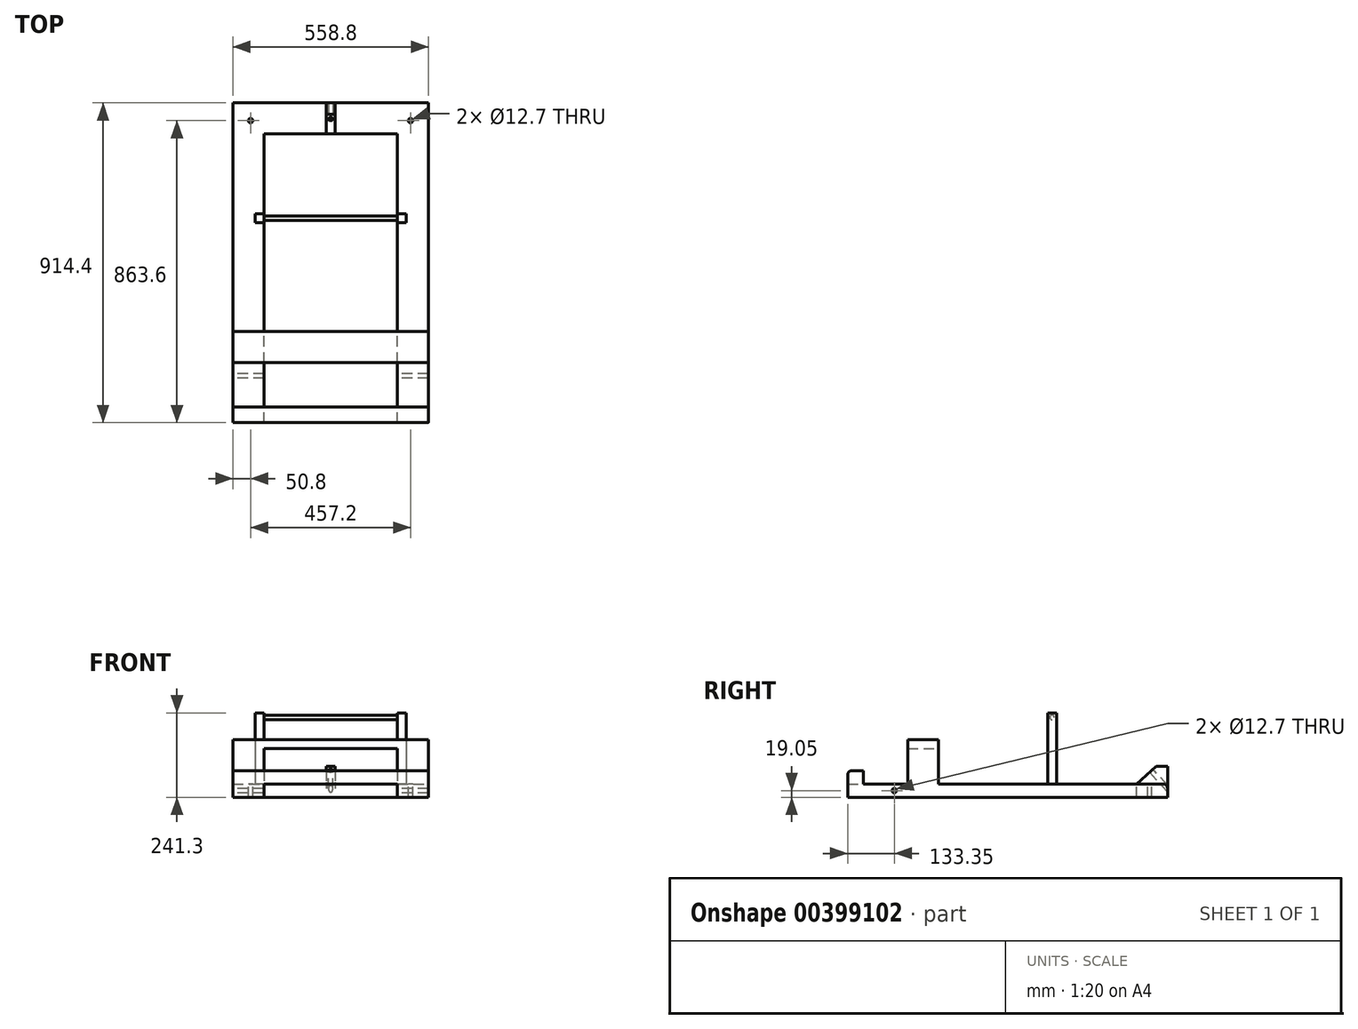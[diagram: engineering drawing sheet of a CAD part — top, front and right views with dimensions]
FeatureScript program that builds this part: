
annotation { "Feature Type Name" : "Feature", "Feature Type Description" : "" }
export const myFeature = defineFeature(function(context is Context, id is Id, definition is map)
    precondition{}
    {
        {
            var Q0;
            Q0=qCreatedBy(makeId("Right.planeOp"),FACE);
            var sketch = newSketch(context, id + "F0", { "sketchPlane" : qUnion([Q0])});
            skLineSegment(sketch, "E0.bottom", {"start": v(0, 0) * mm, "end": v(914.4, 0) * mm});
            skLineSegment(sketch, "E0.top", {"start": v(0, 38.1) * mm, "end": v(914.4, 38.1) * mm});
            skLineSegment(sketch, "E0.left", {"start": v(0, 0) * mm, "end": v(0, 38.1) * mm});
            skLineSegment(sketch, "E0.right", {"start": v(914.4, 0) * mm, "end": v(914.4, 38.1) * mm});
            skSolve(sketch);
        }
        {
            var Q0;
            Q0=makeQuery(id+"F0.imprint","IMPRINT",FACE,{"disambiguationData":[TD([[makeQuery(id+"F0.imprint","IMPRINT",EDGE,{"derivedFrom":sQuery(id+"F0.wireOp",EDGE,"E0.bottom")}),1.0]])]});
            extrude(context, id + "F1", {"entities" : qUnion([Q0]), "depth" : 88.9 * mm});
        }
        {
            var Q0;
            Q0=makeQuery(id+"F1.opExtrude","SWEPT_FACE",FACE,{"disambiguationData":[OSD([sQuery(id+"F0.wireOp",EDGE,"E0.top")])]});
            var sketch = newSketch(context, id + "F2", { "sketchPlane" : qUnion([Q0])});
            skLineSegment(sketch, "E1.bottom", {"start": v(88.9, 0) * mm, "end": v(-469.9, 0) * mm});
            skLineSegment(sketch, "E1.top", {"start": v(88.9, 44.45) * mm, "end": v(-469.9, 44.45) * mm});
            skLineSegment(sketch, "E1.left", {"start": v(88.9, 0) * mm, "end": v(88.9, 44.45) * mm});
            skLineSegment(sketch, "E1.right", {"start": v(-469.9, 0) * mm, "end": v(-469.9, 44.45) * mm});
            skSolve(sketch);
        }
        {
            var Q0;
            {var subQ4=sQuery(id+"F2.wireOp",EDGE,"E1.left");Q0=makeQuery(id+"F2.imprint","IMPRINT",FACE,{"disambiguationData":[TD([[makeQuery(id+"F2.imprint","IMPRINT",EDGE,{"derivedFrom":subQ4}),1.0]])]});}
            var Q1;
            {var subQ3=sQuery(id+"F2.wireOp",EDGE,"E1.right");Q1=makeQuery(id+"F2.imprint","IMPRINT",FACE,{"disambiguationData":[TD([[makeQuery(id+"F2.imprint","IMPRINT",EDGE,{"derivedFrom":subQ3}),-1.0]])]});}
            extrude(context, id + "F3", {"entities" : qUnion([Q0, Q1]), "operationType" : NewBodyOperationType.ADD, "depth" : 38.1 * mm});
        }
        {
            var Q0;
            Q0=makeQuery(id+"F3.opExtrude","CAP_FACE",FACE,{"disambiguationData":[OSD([sQuery(id+"F2.wireOp",EDGE,"E1.bottom"),sQuery(id+"F2.wireOp",EDGE,"E1.top"),sQuery(id+"F2.wireOp",EDGE,"E1.left"),sQuery(id+"F2.wireOp",EDGE,"E1.right")])],"isStart":true});
            var sketch = newSketch(context, id + "F4", { "sketchPlane" : qUnion([Q0])});
            skLineSegment(sketch, "E2.bottom", {"start": v(-469.9, 0) * mm, "end": v(-381, 0) * mm});
            skLineSegment(sketch, "E2.top", {"start": v(-469.9, -914.4) * mm, "end": v(-381, -914.4) * mm});
            skLineSegment(sketch, "E2.left", {"start": v(-469.9, 0) * mm, "end": v(-469.9, -914.4) * mm});
            skLineSegment(sketch, "E2.right", {"start": v(-381, 0) * mm, "end": v(-381, -914.4) * mm});
            skSolve(sketch);
        }
        {
            var Q0;
            {var subQ0=sQuery(id+"F4.wireOp",EDGE,"E2.bottom");Q0=makeQuery(id+"F4.imprint","IMPRINT",FACE,{"disambiguationData":[TD([[makeQuery(id+"F4.imprint","IMPRINT",EDGE,{"derivedFrom":subQ0}),1.0]])]});}
            var Q1;
            {var subQ0=sQuery(id+"F4.wireOp",EDGE,"E2.top");Q1=makeQuery(id+"F4.imprint","IMPRINT",FACE,{"disambiguationData":[TD([[makeQuery(id+"F4.imprint","IMPRINT",EDGE,{"derivedFrom":subQ0}),1.0]])]});}
            extrude(context, id + "F5", {"entities" : qUnion([Q0, Q1]), "operationType" : NewBodyOperationType.ADD, "depth" : 38.1 * mm});
        }
        {
            var Q0;
            Q0=makeQuery(id+"F5.boolean.opBoolean","MERGE",FACE,{"derivedFrom":[makeQuery(id+"F3.opExtrude","SWEPT_FACE",FACE,{"disambiguationData":[OSD([sQuery(id+"F2.wireOp",EDGE,"E1.right")])]}),makeQuery(id+"F5.opExtrude","SWEPT_FACE",FACE,{"disambiguationData":[OSD([sQuery(id+"F4.wireOp",EDGE,"E2.left")])]})]});
            var sketch = newSketch(context, id + "F6", { "sketchPlane" : qUnion([Q0])});
            skCircle(sketch, "E3", {"center": v(-133.35, 19.05) * mm, "radius": 6.35 * mm});
            skSolve(sketch);
        }
        {
            var Q0;
            Q0=makeQuery(id+"F6.imprint","IMPRINT",FACE,{"disambiguationData":[TD([[makeQuery(id+"F6.imprint","IMPRINT",EDGE,{"derivedFrom":sQuery(id+"F6.wireOp",EDGE,"E3")}),1.0]])]});
            var Q1;
            Q1=sQuery(id+"F6.wireOp",EDGE,"E3");
            extrude(context, id + "F7", {"entities" : qUnion([Q0]), "operationType" : NewBodyOperationType.REMOVE, "surfaceEntities" : qUnion([Q1]), "endBound" : BoundingType.THROUGH_ALL, "oppositeDirection" : true, "depth" : 25.4 * mm});
        }
        {
            var Q0;
            Q0=makeQuery(id+"F1.opExtrude","SWEPT_FACE",FACE,{"disambiguationData":[OSD([sQuery(id+"F0.wireOp",EDGE,"E0.top")])]});
            var sketch = newSketch(context, id + "F8", { "sketchPlane" : qUnion([Q0])});
            skSolve(sketch);
        }
        {
            var Q0;
            {var subQ0=sQuery(id+"F0.wireOp",EDGE,"E0.top");Q0=makeQuery(id+"F8.imprint","IMPRINT",FACE,{"disambiguationData":[TD([[makeQuery(id+"F8.imprint","IMPRINT",EDGE,{"derivedFrom":makeQuery(id+"F1.opExtrude","CAP_EDGE",EDGE,{"disambiguationData":[OSD([subQ0])],"isStart":false})}),1.0]])]});}
            var sketch = newSketch(context, id + "F9", { "sketchPlane" : qUnion([Q0])});
            skLineSegment(sketch, "E4.bottom", {"start": v(25.4, 571.5) * mm, "end": v(0, 571.5) * mm});
            skLineSegment(sketch, "E4.top", {"start": v(25.4, 596.9) * mm, "end": v(0, 596.9) * mm});
            skLineSegment(sketch, "E4.left", {"start": v(25.4, 571.5) * mm, "end": v(25.4, 596.9) * mm});
            skLineSegment(sketch, "E4.right", {"start": v(0, 571.5) * mm, "end": v(0, 596.9) * mm});
            skSolve(sketch);
        }
        {
            var Q0;
            Q0=makeQuery(id+"F9.imprint","IMPRINT",FACE,{"disambiguationData":[TD([[makeQuery(id+"F9.imprint","IMPRINT",EDGE,{"derivedFrom":sQuery(id+"F9.wireOp",EDGE,"E4.bottom")}),-1.0]])]});
            extrude(context, id + "F10", {"entities" : qUnion([Q0]), "operationType" : NewBodyOperationType.ADD, "depth" : 203.2 * mm});
        }
        {
            var Q0;
            Q0=makeQuery(id+"F5.opExtrude","CAP_FACE",FACE,{"disambiguationData":[OSD([sQuery(id+"F4.wireOp",EDGE,"E2.bottom"),sQuery(id+"F4.wireOp",EDGE,"E2.top"),sQuery(id+"F4.wireOp",EDGE,"E2.left"),sQuery(id+"F4.wireOp",EDGE,"E2.right")])],"isStart":true});
            var sketch = newSketch(context, id + "F11", { "sketchPlane" : qUnion([Q0])});
            skLineSegment(sketch, "E5.bottom", {"start": v(-381, 571.5) * mm, "end": v(-406.4, 571.5) * mm});
            skLineSegment(sketch, "E5.top", {"start": v(-381, 596.9) * mm, "end": v(-406.4, 596.9) * mm});
            skLineSegment(sketch, "E5.left", {"start": v(-381, 571.5) * mm, "end": v(-381, 596.9) * mm});
            skLineSegment(sketch, "E5.right", {"start": v(-406.4, 571.5) * mm, "end": v(-406.4, 596.9) * mm});
            skSolve(sketch);
        }
        {
            var Q0;
            Q0=makeQuery(id+"F11.imprint","IMPRINT",FACE,{"disambiguationData":[TD([[makeQuery(id+"F11.imprint","IMPRINT",EDGE,{"derivedFrom":sQuery(id+"F11.wireOp",EDGE,"E5.bottom")}),-1.0]])]});
            extrude(context, id + "F12", {"entities" : qUnion([Q0]), "operationType" : NewBodyOperationType.ADD, "depth" : 203.2 * mm});
        }
        {
            var Q0;
            Q0=makeQuery(id+"F10.boolean.opBoolean","MERGE",FACE,{"derivedFrom":[makeQuery(id+"F1.opExtrude","CAP_FACE",FACE,{"disambiguationData":[OSD([sQuery(id+"F0.wireOp",EDGE,"E0.bottom"),sQuery(id+"F0.wireOp",EDGE,"E0.top"),sQuery(id+"F0.wireOp",EDGE,"E0.left"),sQuery(id+"F0.wireOp",EDGE,"E0.right")])],"isStart":true}),makeQuery(id+"F10.opExtrude","SWEPT_FACE",FACE,{"disambiguationData":[OSD([sQuery(id+"F9.wireOp",EDGE,"E4.right")])]})]});
            var sketch = newSketch(context, id + "F13", { "sketchPlane" : qUnion([Q0])});
            skCircle(sketch, "E6", {"center": v(-584.2, 228.6) * mm, "radius": 6.35 * mm});
            skSolve(sketch);
        }
        {
            var Q0;
            Q0=makeQuery(id+"F13.imprint","IMPRINT",FACE,{"disambiguationData":[TD([[makeQuery(id+"F13.imprint","IMPRINT",EDGE,{"derivedFrom":sQuery(id+"F13.wireOp",EDGE,"E6")}),1.0]])]});
            extrude(context, id + "F14", {"entities" : qUnion([Q0]), "operationType" : NewBodyOperationType.ADD, "depth" : 406.4 * mm});
        }
        {
            var Q0;
            Q0=makeQuery(id+"F10.boolean.opBoolean","MERGE",FACE,{"derivedFrom":[makeQuery(id+"F1.opExtrude","CAP_FACE",FACE,{"disambiguationData":[OSD([sQuery(id+"F0.wireOp",EDGE,"E0.bottom"),sQuery(id+"F0.wireOp",EDGE,"E0.top"),sQuery(id+"F0.wireOp",EDGE,"E0.left"),sQuery(id+"F0.wireOp",EDGE,"E0.right")])],"isStart":true}),makeQuery(id+"F10.opExtrude","SWEPT_FACE",FACE,{"disambiguationData":[OSD([sQuery(id+"F9.wireOp",EDGE,"E4.right")])]})]});
            var sketch = newSketch(context, id + "F15", { "sketchPlane" : qUnion([Q0])});
            skLineSegment(sketch, "E7.bottom", {"start": v(-914.4, 0) * mm, "end": v(-825.5, 0) * mm});
            skLineSegment(sketch, "E7.top", {"start": v(-914.4, 38.1) * mm, "end": v(-825.5, 38.1) * mm});
            skLineSegment(sketch, "E7.left", {"start": v(-914.4, 0) * mm, "end": v(-914.4, 38.1) * mm});
            skLineSegment(sketch, "E7.right", {"start": v(-825.5, 0) * mm, "end": v(-825.5, 38.1) * mm});
            skSolve(sketch);
        }
        {
            var Q0;
            Q0=makeQuery(id+"F15.imprint","IMPRINT",FACE,{"disambiguationData":[TD([[makeQuery(id+"F15.imprint","IMPRINT",EDGE,{"derivedFrom":sQuery(id+"F15.wireOp",EDGE,"E7.bottom")}),-1.0]])]});
            extrude(context, id + "F16", {"entities" : qUnion([Q0]), "operationType" : NewBodyOperationType.ADD, "depth" : 381 * mm});
        }
        {
            var Q0;
            {var subQ1=sQuery(id+"F0.wireOp",EDGE,"E0.top");Q0=makeQuery(id+"F8.imprint","IMPRINT",FACE,{"disambiguationData":[TD([[makeQuery(id+"F8.imprint","IMPRINT",EDGE,{"derivedFrom":makeQuery(id+"F1.opExtrude","CAP_EDGE",EDGE,{"disambiguationData":[OSD([subQ1])],"isStart":false})}),1.0]])]});}
            var sketch = newSketch(context, id + "F17", { "sketchPlane" : qUnion([Q0])});
            skCircle(sketch, "E8", {"center": v(-419.1, 863.6) * mm, "radius": 6.35 * mm});
            skCircle(sketch, "E9", {"center": v(38.1, 863.6) * mm, "radius": 6.35 * mm});
            skSolve(sketch);
        }
        {
            var Q0;
            Q0=makeQuery(id+"F17.imprint","IMPRINT",FACE,{"disambiguationData":[TD([[makeQuery(id+"F17.imprint","IMPRINT",EDGE,{"derivedFrom":sQuery(id+"F17.wireOp",EDGE,"E9")}),1.0]])]});
            var Q1;
            Q1=makeQuery(id+"F17.imprint","IMPRINT",FACE,{"disambiguationData":[TD([[makeQuery(id+"F17.imprint","IMPRINT",EDGE,{"derivedFrom":sQuery(id+"F17.wireOp",EDGE,"E8")}),1.0]])]});
            extrude(context, id + "F18", {"entities" : qUnion([Q0, Q1]), "operationType" : NewBodyOperationType.REMOVE, "oppositeDirection" : true, "depth" : 38.1 * mm});
        }
        {
            var Q0;
            Q0=makeQuery(id+"F16.boolean.opBoolean","MERGE",FACE,{"derivedFrom":[makeQuery(id+"F1.opExtrude","SWEPT_FACE",FACE,{"disambiguationData":[OSD([sQuery(id+"F0.wireOp",EDGE,"E0.top")])]}),makeQuery(id+"F5.opExtrude","CAP_FACE",FACE,{"disambiguationData":[OSD([sQuery(id+"F4.wireOp",EDGE,"E2.bottom"),sQuery(id+"F4.wireOp",EDGE,"E2.top"),sQuery(id+"F4.wireOp",EDGE,"E2.left"),sQuery(id+"F4.wireOp",EDGE,"E2.right")])],"isStart":true}),makeQuery(id+"F16.opExtrude","SWEPT_FACE",FACE,{"disambiguationData":[OSD([sQuery(id+"F15.wireOp",EDGE,"E7.top")])]})]});
            var sketch = newSketch(context, id + "F19", { "sketchPlane" : qUnion([Q0])});
            skLineSegment(sketch, "E10.bottom", {"start": v(-203.2, 825.5) * mm, "end": v(-177.8, 825.5) * mm});
            skLineSegment(sketch, "E10.top", {"start": v(-203.2, 914.4) * mm, "end": v(-177.8, 914.4) * mm});
            skLineSegment(sketch, "E10.left", {"start": v(-203.2, 825.5) * mm, "end": v(-203.2, 914.4) * mm});
            skLineSegment(sketch, "E10.right", {"start": v(-177.8, 825.5) * mm, "end": v(-177.8, 914.4) * mm});
            skSolve(sketch);
        }
        {
            var Q0;
            Q0=makeQuery(id+"F19.imprint","IMPRINT",FACE,{"disambiguationData":[TD([[makeQuery(id+"F19.imprint","IMPRINT",EDGE,{"derivedFrom":sQuery(id+"F19.wireOp",EDGE,"E10.bottom")}),1.0]])]});
            extrude(context, id + "F20", {"entities" : qUnion([Q0]), "operationType" : NewBodyOperationType.ADD, "depth" : 50.8 * mm});
        }
        {
            var Q0;
            {var subQ0=sQuery(id+"F0.wireOp",EDGE,"E0.right");var subQ2=sQuery(id+"F4.wireOp",EDGE,"E2.top");var subQ3=sQuery(id+"F0.wireOp",EDGE,"E0.top");var subQ4=sQuery(id+"F15.wireOp",EDGE,"E7.top");var subQ5=sQuery(id+"F15.wireOp",EDGE,"E7.left");Q0=makeQuery(id+"F20.boolean.opBoolean","SPLIT",EDGE,{"disambiguationData":[TD([makeQuery(id+"F3.opExtrude","SWEPT_FACE",FACE,{"disambiguationData":[OSD([sQuery(id+"F2.wireOp",EDGE,"E1.right")])]})])],"derivedFrom":makeQuery(id+"F16.boolean.opBoolean","MERGE",EDGE,{"derivedFrom":[makeQuery(id+"F1.opExtrude","SWEPT_EDGE",EDGE,{"disambiguationData":[OSD([subQ3,subQ0])]}),makeQuery(id+"F5.opExtrude","CAP_EDGE",EDGE,{"disambiguationData":[OSD([subQ2])],"isStart":true}),makeQuery(id+"F16.opExtrude","SWEPT_EDGE",EDGE,{"disambiguationData":[OSD([subQ4,subQ5])]})]})});}
            var Q1;
            {var subQ0=sQuery(id+"F0.wireOp",EDGE,"E0.right");var subQ1=sQuery(id+"F0.wireOp",EDGE,"E0.top");var subQ2=sQuery(id+"F4.wireOp",EDGE,"E2.top");var subQ3=sQuery(id+"F15.wireOp",EDGE,"E7.top");var subQ4=sQuery(id+"F15.wireOp",EDGE,"E7.left");Q1=makeQuery(id+"F20.boolean.opBoolean","SPLIT",EDGE,{"disambiguationData":[TD([makeQuery(id+"F3.opExtrude","SWEPT_FACE",FACE,{"disambiguationData":[OSD([sQuery(id+"F2.wireOp",EDGE,"E1.left")])]})])],"derivedFrom":makeQuery(id+"F16.boolean.opBoolean","MERGE",EDGE,{"derivedFrom":[makeQuery(id+"F1.opExtrude","SWEPT_EDGE",EDGE,{"disambiguationData":[OSD([subQ1,subQ0])]}),makeQuery(id+"F5.opExtrude","CAP_EDGE",EDGE,{"disambiguationData":[OSD([subQ2])],"isStart":true}),makeQuery(id+"F16.opExtrude","SWEPT_EDGE",EDGE,{"disambiguationData":[OSD([subQ3,subQ4])]})]})});}
            var Q2;
            Q2=makeQuery(id+"F3.opExtrude","CAP_EDGE",EDGE,{"disambiguationData":[OSD([sQuery(id+"F2.wireOp",EDGE,"E1.bottom")])],"isStart":false});
            fillet(context, id + "F21", {"entities" : qUnion([Q0, Q1, Q2]), "radius" : 12.7 * mm, "tangentPropagation" : true, "allowEdgeOverflow" : false});
        }
        {
            var Q0;
            Q0=makeQuery(id+"F20.opExtrude","SWEPT_FACE",FACE,{"disambiguationData":[OSD([sQuery(id+"F19.wireOp",EDGE,"E10.left")])]});
            var sketch = newSketch(context, id + "F22", { "sketchPlane" : qUnion([Q0])});
            skLineSegment(sketch, "E11", {"start": v(-882.15, 88.9) * mm, "end": v(-825.5, 38.1) * mm});
            skSolve(sketch);
        }
        {
            var Q0;
            {var subQ0=sQuery(id+"F22.wireOp",EDGE,"E11");Q0=makeQuery(id+"F22.imprint","IMPRINT",FACE,{"disambiguationData":[TD([[makeQuery(id+"F22.imprint","IMPRINT",EDGE,{"derivedFrom":subQ0}),1.0]])]});}
            extrude(context, id + "F23", {"entities" : qUnion([Q0]), "operationType" : NewBodyOperationType.REMOVE, "oppositeDirection" : true, "depth" : 25.4 * mm});
        }
        {
            var Q0;
            Q0=makeQuery(id+"F23.boolean.opBoolean","COPY",FACE,{"derivedFrom":makeQuery(id+"F23.opExtrude","SWEPT_FACE",FACE,{"disambiguationData":[OSD([sQuery(id+"F22.wireOp",EDGE,"E11")])]})});
            var sketch = newSketch(context, id + "F24", { "sketchPlane" : qUnion([Q0])});
            skCircle(sketch, "E12", {"center": v(-190.5, 697.04) * mm, "radius": 6.35 * mm});
            skSolve(sketch);
        }
        {
            var Q0;
            Q0=makeQuery(id+"F24.imprint","IMPRINT",FACE,{"disambiguationData":[TD([[makeQuery(id+"F24.imprint","IMPRINT",EDGE,{"derivedFrom":sQuery(id+"F24.wireOp",EDGE,"E12")}),1.0]])]});
            extrude(context, id + "F25", {"entities" : qUnion([Q0]), "operationType" : NewBodyOperationType.REMOVE, "oppositeDirection" : true, "depth" : 101.6 * mm});
        }
        {
            var Q0;
            {var subQ0=sQuery(id+"F2.wireOp",EDGE,"E1.right");var subQ2=sQuery(id+"F4.wireOp",EDGE,"E2.right");var subQ3=sQuery(id+"F4.wireOp",EDGE,"E2.left");var subQ4=sQuery(id+"F4.wireOp",EDGE,"E2.top");Q0=makeQuery(id+"F20.boolean.opBoolean","SPLIT",FACE,{"disambiguationData":[TD([makeQuery(id+"F3.opExtrude","SWEPT_FACE",FACE,{"disambiguationData":[OSD([subQ0])]})])],"derivedFrom":makeQuery(id+"F16.boolean.opBoolean","MERGE",FACE,{"derivedFrom":[makeQuery(id+"F1.opExtrude","SWEPT_FACE",FACE,{"disambiguationData":[OSD([sQuery(id+"F0.wireOp",EDGE,"E0.top")])]}),makeQuery(id+"F5.opExtrude","CAP_FACE",FACE,{"disambiguationData":[OSD([sQuery(id+"F4.wireOp",EDGE,"E2.bottom"),subQ4,subQ3,subQ2])],"isStart":true}),makeQuery(id+"F16.opExtrude","SWEPT_FACE",FACE,{"disambiguationData":[OSD([sQuery(id+"F15.wireOp",EDGE,"E7.top")])]})]})});}
            var sketch = newSketch(context, id + "F26", { "sketchPlane" : qUnion([Q0])});
            skLineSegment(sketch, "E13.bottom", {"start": v(-469.9, 260.35) * mm, "end": v(-381, 260.35) * mm});
            skLineSegment(sketch, "E13.top", {"start": v(-469.9, 171.45) * mm, "end": v(-381, 171.45) * mm});
            skLineSegment(sketch, "E13.left", {"start": v(-469.9, 260.35) * mm, "end": v(-469.9, 171.45) * mm});
            skLineSegment(sketch, "E13.right", {"start": v(-381, 260.35) * mm, "end": v(-381, 171.45) * mm});
            skLineSegment(sketch, "E14.bottom", {"start": v(0, 171.45) * mm, "end": v(88.9, 171.45) * mm});
            skLineSegment(sketch, "E14.top", {"start": v(0, 260.35) * mm, "end": v(88.9, 260.35) * mm});
            skLineSegment(sketch, "E14.left", {"start": v(0, 171.45) * mm, "end": v(0, 260.35) * mm});
            skLineSegment(sketch, "E14.right", {"start": v(88.9, 171.45) * mm, "end": v(88.9, 260.35) * mm});
            skSolve(sketch);
        }
        {
            var Q0;
            Q0=qSketchRegion(id+"F26",true);
            extrude(context, id + "F27", {"entities" : qUnion([Q0]), "operationType" : NewBodyOperationType.ADD, "depth" : 101.6 * mm});
        }
        {
            var Q0;
            Q0=makeQuery(id+"F27.opExtrude","CAP_FACE",FACE,{"disambiguationData":[OSD([sQuery(id+"F26.wireOp",EDGE,"E13.bottom"),sQuery(id+"F26.wireOp",EDGE,"E13.top"),sQuery(id+"F26.wireOp",EDGE,"E13.left"),sQuery(id+"F26.wireOp",EDGE,"E13.right")])],"isStart":false});
            var sketch = newSketch(context, id + "F28", { "sketchPlane" : qUnion([Q0])});
            skLineSegment(sketch, "E15.bottom", {"start": v(-469.9, 260.35) * mm, "end": v(88.9, 260.35) * mm});
            skLineSegment(sketch, "E15.top", {"start": v(-469.9, 171.45) * mm, "end": v(88.9, 171.45) * mm});
            skLineSegment(sketch, "E15.left", {"start": v(-469.9, 260.35) * mm, "end": v(-469.9, 171.45) * mm});
            skLineSegment(sketch, "E15.right", {"start": v(88.9, 260.35) * mm, "end": v(88.9, 171.45) * mm});
            skSolve(sketch);
        }
        {
            var Q0;
            {var subQ2=sQuery(id+"F28.wireOp",EDGE,"E15.right");Q0=makeQuery(id+"F28.imprint","IMPRINT",FACE,{"disambiguationData":[TD([[makeQuery(id+"F28.imprint","IMPRINT",EDGE,{"derivedFrom":subQ2}),-1.0]])]});}
            var Q1;
            Q1=qSketchRegion(id+"F28",true);
            extrude(context, id + "F29", {"entities" : qUnion([Q0, Q1]), "operationType" : NewBodyOperationType.ADD, "depth" : 25.4 * mm});
        }
    });
